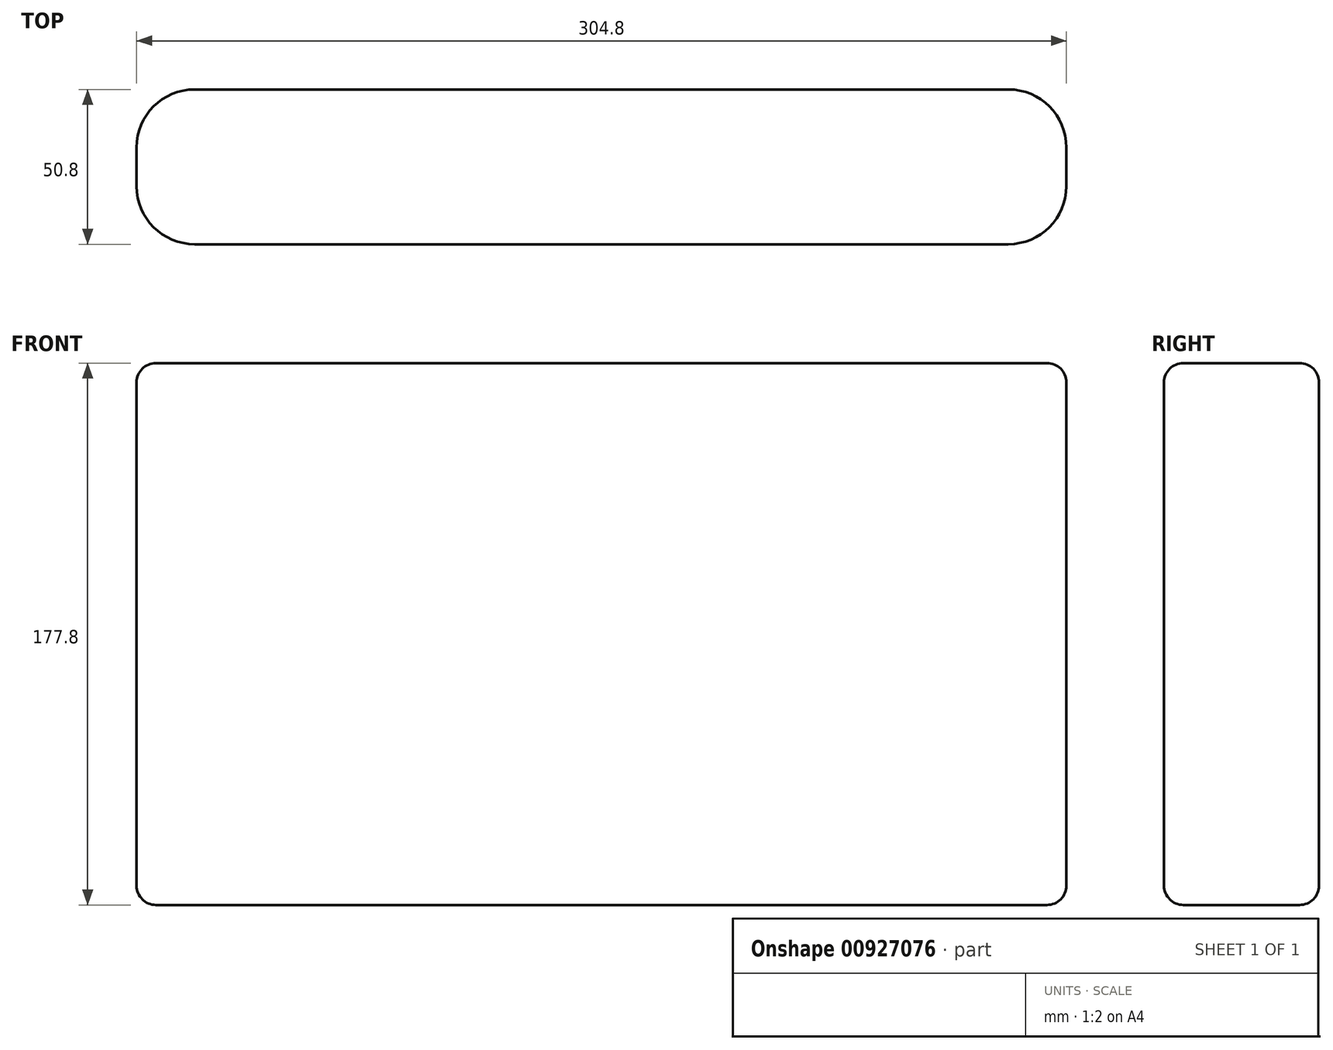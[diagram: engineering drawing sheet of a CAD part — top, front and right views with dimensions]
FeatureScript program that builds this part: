
annotation { "Feature Type Name" : "Feature", "Feature Type Description" : "" }
export const myFeature = defineFeature(function(context is Context, id is Id, definition is map)
    precondition{}
    {
        {
            var Q0;
            Q0=qCreatedBy(makeId("Front.planeOp"),FACE);
            var sketch = newSketch(context, id + "F0", { "sketchPlane" : qUnion([Q0])});
            skLineSegment(sketch, "E0", {"start": v(0, 0) * mm, "end": v(304.8, 0) * mm});
            skLineSegment(sketch, "E1", {"start": v(304.8, 0) * mm, "end": v(304.8, 177.8) * mm});
            skLineSegment(sketch, "E2", {"start": v(304.8, 177.8) * mm, "end": v(0, 177.8) * mm});
            skLineSegment(sketch, "E3", {"start": v(0, 177.8) * mm, "end": v(0, 0) * mm});
            skSolve(sketch);
        }
        {
            var Q0;
            Q0=makeQuery(id+"F0.imprint","IMPRINT",FACE,{"disambiguationData":[TD([[makeQuery(id+"F0.imprint","IMPRINT",EDGE,{"derivedFrom":sQuery(id+"F0.wireOp",EDGE,"E0")}),1.0]])]});
            extrude(context, id + "F1", {"entities" : qUnion([Q0]), "endBound" : BoundingType.SYMMETRIC, "depth" : 50.8 * mm, "offsetDistance" : 25.4 * mm});
        }
        {
            var Q0;
            Q0=makeQuery(id+"F1.opExtrude","CAP_EDGE",EDGE,{"disambiguationData":[OSD([sQuery(id+"F0.wireOp",EDGE,"E1")])],"isStart":false});
            var Q1;
            Q1=makeQuery(id+"F1.opExtrude","CAP_EDGE",EDGE,{"disambiguationData":[OSD([sQuery(id+"F0.wireOp",EDGE,"E1")])],"isStart":true});
            var Q2;
            Q2=makeQuery(id+"F1.opExtrude","CAP_EDGE",EDGE,{"disambiguationData":[OSD([sQuery(id+"F0.wireOp",EDGE,"E3")])],"isStart":true});
            var Q3;
            Q3=makeQuery(id+"F1.opExtrude","CAP_EDGE",EDGE,{"disambiguationData":[OSD([sQuery(id+"F0.wireOp",EDGE,"E3")])],"isStart":false});
            fillet(context, id + "F2", {"entities" : qUnion([Q0, Q1, Q2, Q3]), "radius" : 19.05 * mm, "tangentPropagation" : true, "allowEdgeOverflow" : false});
        }
        {
            var Q0;
            Q0=makeQuery(id+"F1.opExtrude","CAP_EDGE",EDGE,{"disambiguationData":[OSD([sQuery(id+"F0.wireOp",EDGE,"E2")])],"isStart":false});
            var Q1;
            Q1=makeQuery(id+"F1.opExtrude","CAP_EDGE",EDGE,{"disambiguationData":[OSD([sQuery(id+"F0.wireOp",EDGE,"E0")])],"isStart":false});
            fillet(context, id + "F3", {"entities" : qUnion([Q0, Q1]), "radius" : 6.35 * mm, "tangentPropagation" : true, "allowEdgeOverflow" : false});
        }
    });
